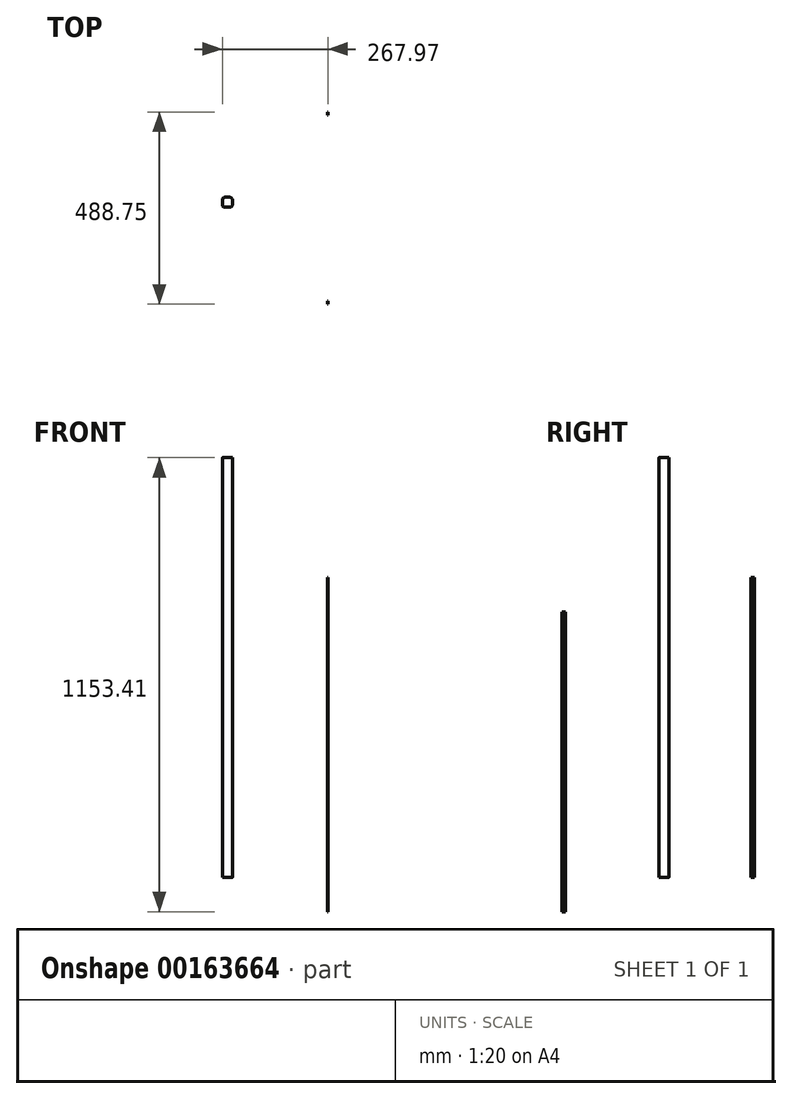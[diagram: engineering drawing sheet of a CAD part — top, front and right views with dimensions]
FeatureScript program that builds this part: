
annotation { "Feature Type Name" : "Feature", "Feature Type Description" : "" }
export const myFeature = defineFeature(function(context is Context, id is Id, definition is map)
    precondition{}
    {
        {
            var Q0;
            Q0=qCreatedBy(makeId("Top.planeOp"),FACE);
            var sketch = newSketch(context, id + "F0", { "sketchPlane" : qUnion([Q0])});
            skLineSegment(sketch, "E0.bottom", {"start": v(6.35, 12.7) * mm, "end": v(-6.35, 12.7) * mm});
            skLineSegment(sketch, "E0.top", {"start": v(6.35, -12.7) * mm, "end": v(-6.35, -12.7) * mm});
            skLineSegment(sketch, "E0.left", {"start": v(12.7, 6.35) * mm, "end": v(12.7, -6.35) * mm});
            skLineSegment(sketch, "E0.right", {"start": v(-12.7, 6.35) * mm, "end": v(-12.7, -6.35) * mm});
            skPoint(sketch, "E0.middle", {"position": v(0, 0) * mm});
            skPoint(sketch, "E1.visualSharp", {"position": v(-12.7, 12.7) * mm});
            skArc(sketch, "E1.filletArc", {"start": v(-6.35, 12.7) * mm, "mid": v(-10.84, 10.84) * mm, "end": v(-12.7, 6.35) * mm});
            skPoint(sketch, "E2.visualSharp", {"position": v(-12.7, -12.7) * mm});
            skArc(sketch, "E2.filletArc", {"start": v(-12.7, -6.35) * mm, "mid": v(-10.84, -10.84) * mm, "end": v(-6.35, -12.7) * mm});
            skPoint(sketch, "E3.visualSharp", {"position": v(12.7, -12.7) * mm});
            skArc(sketch, "E3.filletArc", {"start": v(6.35, -12.7) * mm, "mid": v(10.84, -10.84) * mm, "end": v(12.7, -6.35) * mm});
            skPoint(sketch, "E4.visualSharp", {"position": v(12.7, 12.7) * mm});
            skArc(sketch, "E4.filletArc", {"start": v(12.7, 6.35) * mm, "mid": v(10.84, 10.84) * mm, "end": v(6.35, 12.7) * mm});
            skSolve(sketch);
        }
        {
            var Q0;
            Q0=qSketchRegion(id+"F0",true);
            extrude(context, id + "F1", {"entities" : qUnion([Q0]), "depth" : 1066.8 * mm, "offsetDistance" : 25.4 * mm});
        }
        {
            var Q0;
            Q0=qCreatedBy(makeId("Right.planeOp"),FACE);
            var sketch = newSketch(context, id + "F2", { "sketchPlane" : qUnion([Q0])});
            skLineSegment(sketch, "E5.bottom", {"start": v(-259, 675.39) * mm, "end": v(-250.53, 675.39) * mm});
            skLineSegment(sketch, "E5.top", {"start": v(-259, -86.61) * mm, "end": v(-250.53, -86.61) * mm});
            skLineSegment(sketch, "E5.left", {"start": v(-259, 675.39) * mm, "end": v(-259, -86.61) * mm});
            skLineSegment(sketch, "E5.right", {"start": v(-250.53, 675.39) * mm, "end": v(-250.53, -86.61) * mm});
            skSolve(sketch);
        }
        {
            var Q0;
            Q0=makeQuery(id+"F2.imprint","IMPRINT",FACE,{"disambiguationData":[TD([[makeQuery(id+"F2.imprint","IMPRINT",EDGE,{"derivedFrom":sQuery(id+"F2.wireOp",EDGE,"E5.bottom")}),-1.0]])]});
            extrude(context, id + "F3", {"entities" : qUnion([Q0]), "depth" : 1.27 * mm});
        }
        {
            var Q0;
            Q0=qCreatedBy(makeId("Right.planeOp"),FACE);
            var sketch = newSketch(context, id + "F4", { "sketchPlane" : qUnion([Q0])});
            skLineSegment(sketch, "E6.bottom", {"start": v(221.29, 762) * mm, "end": v(229.75, 762) * mm});
            skLineSegment(sketch, "E6.top", {"start": v(221.29, 0) * mm, "end": v(229.75, 0) * mm});
            skLineSegment(sketch, "E6.left", {"start": v(221.29, 762) * mm, "end": v(221.29, 0) * mm});
            skLineSegment(sketch, "E6.right", {"start": v(229.75, 762) * mm, "end": v(229.75, 0) * mm});
            skSolve(sketch);
        }
        {
            var Q0;
            Q0=makeQuery(id+"F4.imprint","IMPRINT",FACE,{"disambiguationData":[TD([[makeQuery(id+"F4.imprint","IMPRINT",EDGE,{"derivedFrom":sQuery(id+"F4.wireOp",EDGE,"E6.bottom")}),-1.0]])]});
            var Q1;
            Q1=sQuery(id+"F4.wireOp",EDGE,"E6.right");
            var Q2;
            Q2=sQuery(id+"F4.wireOp",EDGE,"E6.left");
            var Q3;
            Q3=sQuery(id+"F4.wireOp",EDGE,"E6.top");
            var Q4;
            Q4=sQuery(id+"F4.wireOp",EDGE,"E6.bottom");
            extrude(context, id + "F5", {"entities" : qUnion([Q0]), "surfaceEntities" : qUnion([Q1, Q2, Q3, Q4]), "depth" : 1.27 * mm});
        }
        {
            var Q0;
            Q0=makeQuery(id+"F3.opExtrude","SWEPT_BODY",BODY,{"disambiguationData":[OSD([sQuery(id+"F2.wireOp",EDGE,"E5.bottom"),sQuery(id+"F2.wireOp",EDGE,"E5.top"),sQuery(id+"F2.wireOp",EDGE,"E5.left"),sQuery(id+"F2.wireOp",EDGE,"E5.right")])]});
            var Q1;
            Q1=makeQuery(id+"F5.opExtrude","SWEPT_BODY",BODY,{"disambiguationData":[OSD([sQuery(id+"F4.wireOp",EDGE,"E6.bottom"),sQuery(id+"F4.wireOp",EDGE,"E6.top"),sQuery(id+"F4.wireOp",EDGE,"E6.left"),sQuery(id+"F4.wireOp",EDGE,"E6.right")])]});
            transform(context, id + "F6", {"entities" : qUnion([Q0, Q1]), "transformType" : TransformType.TRANSLATION_3D, "dx" : 254 * mm, "dy" : 0 * mm, "dz" : 0 * mm, "makeCopy" : false});
        }
    });
